# Revit family: LG_Multi_F_R32_ODU_2Port_U24A_NA_v1.1
name_source: partatom
category: Mechanical Equipment
units: mm (PartAtom-declared; Revit-internal decimal feet)

## family parameters
Always vertical = Yes
Classification = None
Cut with Voids When Loaded = No
Part Type = Normal
Room Calculation Point = No
Round Connector Dimension = Use Diameter
Shared = No
Work Plane-Based = No

## types (1)
- KUMXB181A
    Chassis name = U24A
    Compressor Motor Output (W) = -
    Compressor Type = Twin Rotary
    Cooling Capacity (Btu/h) = 18,000
    Cooling Capacity (kW) = 5.28
    Default Elevation = 0"
    Dimensions (WxHxD)(inch) = 34-1/4 x 25-19/32 x 13
    Dimensions (WxHxD)(mm) = 870 x 650 x 330
    Expansion Valve Type = Electronic Expansion Valve
    Fan Air Flow Rate (CFM) = 85 x 1
    Fan Air Flow Rate (CMM) = -
    Fan Motor Output (W) = 85 x 1
    Fan Motor Type = BLDC
    Fan Type = Propeller
    Heating Capacity (Btu/h) = 20,000
    Heating Capacity (kW) = 5.86
    Model name (Buyer) = KUMXB181A
    Model name (Factory) = Z2UR18GFA0
    Net Weight (kg) = 46.6
    Net Weight (lbs) = 102.7
    Pipe Connection_Gas Side (inch) = 3/8 x 2
    Pipe Connection_Gas Side (mm) = 9.52 x 2
    Pipe Connection_Liquid Side (inch) = 1/4 x 2
    Pipe Connection_Liquid Side (mm) = 6.35 x 2
    Power Input (Cooling)(kW) = 1.33
    Power Input (Heating)(kW) = 1.79
    Power Supply (Ph_V_Hz) = 1, 208/230, 60
    Power Supply Cable = 18 x 3C
    Refrigerant Charge (g) = 1402(3.090lbs)
    Refrigerant Gas Connection Diameter = 3/8"
    Refrigerant Liquid Connection Diameter = 1/4"
    Refrigerant Type = R32
    Running Current (Cooling)(A) = 6.10
    Running Current (Heating)(A) = 8.20
    Sound Power Level Cooling (dB(A)) = -
    Sound Power Level Heating (dB(A)) = -
    Sound Pressure Level Cooling (dB(A)) = 49
    Sound Pressure Level Heating (dB(A)) = 54
    Temp Operating Range (Cooling)(C) = -
    Temp Operating Range (Cooling)(F) = 14 ~ 118.4
    Temp Operating Range (Heating)(C) = -
    Temp Operating Range (Heating)(F) = -4 ~ 64.4
    Type = Multi F R32
